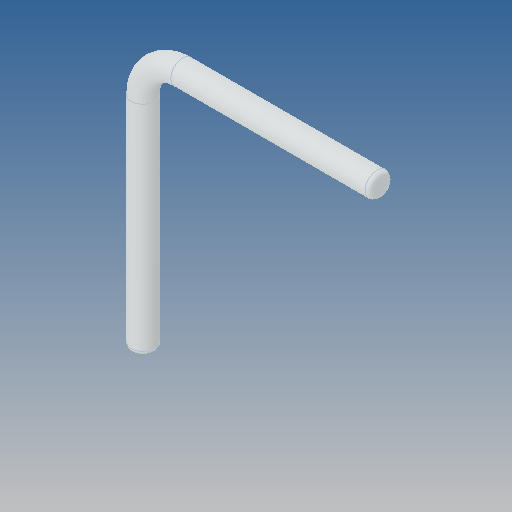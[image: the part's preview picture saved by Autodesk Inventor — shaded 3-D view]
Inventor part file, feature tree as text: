
AUTODESK INVENTOR PART (.ipt)
format: ipt  version: 2020 (Build 240168000, 168)  size: 99,840 bytes
history: mixed  units: mm
features: other x1, fillet x1, imported_body x1
ambient origin geometry x8: Origin, YZ Plane, XZ Plane, XY Plane, X Axis, Y Axis, Z Axis, Center Point
bodies: Body1 (imported_parasolid)
feature tree (3):
  other  "Твердое тело1"
  fillet  "Fillet1"  [1 undecoded]
  imported_body  NMx_Import_Brep_tag  [imported B-rep: ~7 faces, bbox_mm=[6.0, 6.8, 0.3]]
note: 1 required parameter value undecoded (feature->parameter linkage not recoverable at this tier; creation-order binding heuristic only, values carry confidence <= 0.55)
